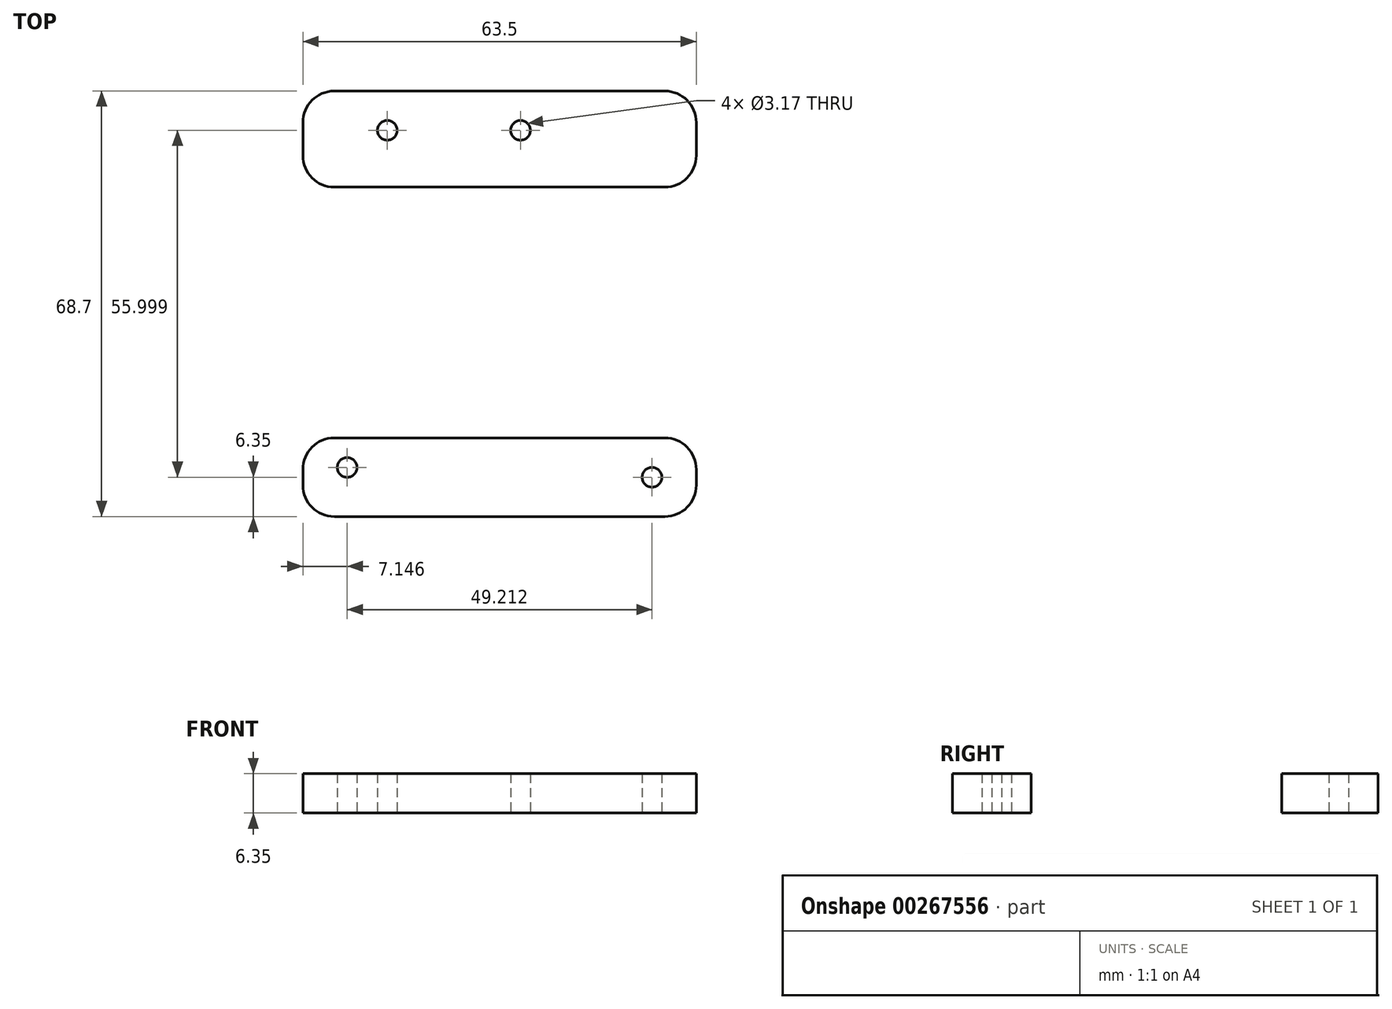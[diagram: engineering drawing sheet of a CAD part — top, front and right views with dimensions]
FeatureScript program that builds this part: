
annotation { "Feature Type Name" : "Feature", "Feature Type Description" : "" }
export const myFeature = defineFeature(function(context is Context, id is Id, definition is map)
    precondition{}
    {
        {
            var Q0;
            Q0=qCreatedBy(makeId("Top.planeOp"),FACE);
            var sketch = newSketch(context, id + "F0", { "sketchPlane" : qUnion([Q0])});
            skLineSegment(sketch, "E0.bottom", {"start": v(-41.62, 0) * mm, "end": v(21.88, 0) * mm});
            skLineSegment(sketch, "E0.top", {"start": v(-41.62, 12.7) * mm, "end": v(21.88, 12.7) * mm});
            skLineSegment(sketch, "E0.left", {"start": v(-41.62, 0) * mm, "end": v(-41.62, 12.7) * mm});
            skLineSegment(sketch, "E0.right", {"start": v(21.88, 0) * mm, "end": v(21.88, 12.7) * mm});
            skCircle(sketch, "E1", {"center": v(14.74, 6.35) * mm, "radius": 1.59 * mm});
            skCircle(sketch, "E2", {"center": v(-34.47, 7.94) * mm, "radius": 1.59 * mm});
            skLineSegment(sketch, "E3", {"start": v(14.74, 6.35) * mm, "end": v(-34.47, 6.35) * mm});
            skLineSegment(sketch, "E4", {"start": v(-34.47, 6.35) * mm, "end": v(-34.47, 7.94) * mm});
            skLineSegment(sketch, "E5.bottom", {"start": v(-41.62, 68.7) * mm, "end": v(21.88, 68.7) * mm});
            skLineSegment(sketch, "E5.top", {"start": v(-41.62, 53.18) * mm, "end": v(21.88, 53.18) * mm});
            skLineSegment(sketch, "E5.left", {"start": v(-41.62, 68.7) * mm, "end": v(-41.62, 53.18) * mm});
            skLineSegment(sketch, "E5.right", {"start": v(21.88, 68.7) * mm, "end": v(21.88, 53.18) * mm});
            skCircle(sketch, "E6", {"center": v(-6.49, 62.35) * mm, "radius": 1.59 * mm});
            skCircle(sketch, "E7", {"center": v(-27.99, 62.35) * mm, "radius": 1.59 * mm});
            skLineSegment(sketch, "E8.bottom", {"start": v(-27.99, 53.18) * mm, "end": v(-6.49, 53.18) * mm});
            skLineSegment(sketch, "E8.top", {"start": v(-27.99, 12.7) * mm, "end": v(-6.49, 12.7) * mm});
            skLineSegment(sketch, "E8.left", {"start": v(-27.99, 53.18) * mm, "end": v(-27.99, 12.7) * mm});
            skLineSegment(sketch, "E8.right", {"start": v(-6.49, 53.18) * mm, "end": v(-6.49, 12.7) * mm});
            skSolve(sketch);
        }
        {
            var Q0;
            Q0=makeQuery(id+"F0.imprint","IMPRINT",FACE,{"disambiguationData":[TD([[makeQuery(id+"F0.imprint","IMPRINT",EDGE,{"derivedFrom":sQuery(id+"F0.wireOp",EDGE,"E5.bottom")}),-1.0]])]});
            var Q1;
            Q1=makeQuery(id+"F0.imprint","IMPRINT",FACE,{"disambiguationData":[TD([[makeQuery(id+"F0.imprint","IMPRINT",EDGE,{"derivedFrom":sQuery(id+"F0.wireOp",EDGE,"E8.bottom")}),-1.0]])]});
            var Q2;
            Q2=makeQuery(id+"F0.imprint","IMPRINT",FACE,{"disambiguationData":[TD([[makeQuery(id+"F0.imprint","IMPRINT",EDGE,{"derivedFrom":sQuery(id+"F0.wireOp",EDGE,"E0.bottom")}),1.0]])]});
            extrude(context, id + "F1", {"entities" : qUnion([Q0, Q1, Q2]), "depth" : 6.35 * mm});
        }
        {
            var Q0;
            Q0=makeQuery(id+"F1.opExtrude","SWEPT_EDGE",EDGE,{"disambiguationData":[OSD([sQuery(id+"F0.wireOp",EDGE,"E0.bottom"),sQuery(id+"F0.wireOp",EDGE,"E0.right")])]});
            var Q1;
            Q1=makeQuery(id+"F1.opExtrude","SWEPT_EDGE",EDGE,{"disambiguationData":[OSD([sQuery(id+"F0.wireOp",EDGE,"E0.top"),sQuery(id+"F0.wireOp",EDGE,"E0.right")])]});
            var Q2;
            Q2=makeQuery(id+"F1.opExtrude","SWEPT_EDGE",EDGE,{"disambiguationData":[OSD([sQuery(id+"F0.wireOp",EDGE,"E0.bottom"),sQuery(id+"F0.wireOp",EDGE,"E0.left")])]});
            var Q3;
            Q3=makeQuery(id+"F1.opExtrude","SWEPT_EDGE",EDGE,{"disambiguationData":[OSD([sQuery(id+"F0.wireOp",EDGE,"E0.top"),sQuery(id+"F0.wireOp",EDGE,"E0.left")])]});
            var Q4;
            Q4=makeQuery(id+"F1.opExtrude","SWEPT_EDGE",EDGE,{"disambiguationData":[OSD([sQuery(id+"F0.wireOp",EDGE,"E5.top"),sQuery(id+"F0.wireOp",EDGE,"E5.right")])]});
            var Q5;
            Q5=makeQuery(id+"F1.opExtrude","SWEPT_EDGE",EDGE,{"disambiguationData":[OSD([sQuery(id+"F0.wireOp",EDGE,"E5.bottom"),sQuery(id+"F0.wireOp",EDGE,"E5.right")])]});
            var Q6;
            Q6=makeQuery(id+"F1.opExtrude","SWEPT_EDGE",EDGE,{"disambiguationData":[OSD([sQuery(id+"F0.wireOp",EDGE,"E5.top"),sQuery(id+"F0.wireOp",EDGE,"E5.left")])]});
            var Q7;
            Q7=makeQuery(id+"F1.opExtrude","SWEPT_EDGE",EDGE,{"disambiguationData":[OSD([sQuery(id+"F0.wireOp",EDGE,"E5.bottom"),sQuery(id+"F0.wireOp",EDGE,"E5.left")])]});
            fillet(context, id + "F2", {"entities" : qUnion([Q0, Q1, Q2, Q3, Q4, Q5, Q6, Q7]), "radius" : 5.08 * mm, "tangentPropagation" : true, "allowEdgeOverflow" : false});
        }
    });
